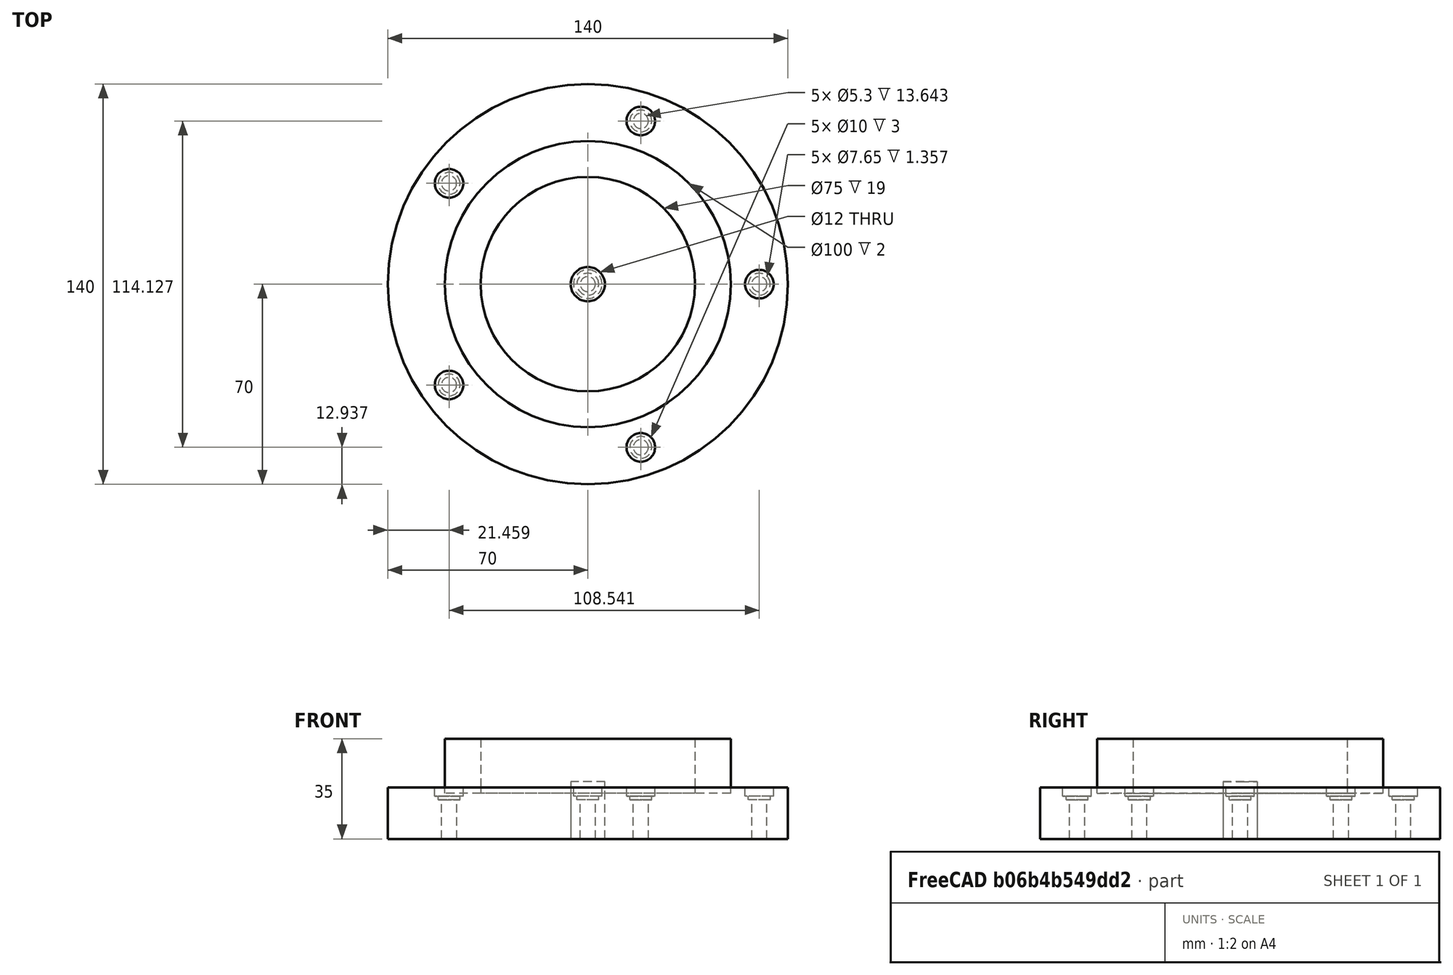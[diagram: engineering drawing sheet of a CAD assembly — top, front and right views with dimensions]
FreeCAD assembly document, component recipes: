
FREECAD ASSEMBLY — COMPONENT RECIPES ("composit_stand3_basement_bearing_holder_model")

This assembly document has 3 components, labeled P0..P2 below (a component is one placed body or linked part). 3 of them carry a construction recipe — the FreeCAD feature program that regenerates the part from scratch, quoted from this document or its linked companion documents; the rest are supplied as boundary geometry only. No exploded tour is included for this assembly.
COMPONENT P0 — recipe-attached ("Body", modeled in this document).
Construction recipe (the document's own serialized feature program — sketch geometry with constraints, then the solid features built on it; lengths are millimeters unless a unit is written):

FEATURE [Sketcher::SketchObject] Sketch
  ArcFitTolerance = 0
  AttachmentSupport = -> [XZ_Plane001]
  FullyConstrained = true
  MakeInternals = false
  MapMode = 5
  Placement = pos=(0,0,0) rot=(1,0,0;1.5708rad)
  sketch-geometry (9):
    g0: LineSegment StartX=0 StartY=0 StartZ=0 EndX=2.65 EndY=0 EndZ=0
    g1: LineSegment StartX=2.65 StartY=0 StartZ=0 EndX=2.65 EndY=13.6432 EndZ=0
    g2: LineSegment StartX=2.65 StartY=13.6432 StartZ=0 EndX=3.825 EndY=13.6432 EndZ=0
    g3: LineSegment StartX=3.825 StartY=13.6432 StartZ=0 EndX=3.825 EndY=15 EndZ=0
    g4: LineSegment StartX=3.825 StartY=15 StartZ=0 EndX=5 EndY=15 EndZ=0
    g5: LineSegment StartX=5 StartY=15 StartZ=0 EndX=5 EndY=18 EndZ=0
    g6: LineSegment StartX=5 StartY=18 StartZ=0 EndX=0 EndY=18 EndZ=0
    g7: LineSegment StartX=0 StartY=18 StartZ=0 EndX=0 EndY=0 EndZ=0
    g8: LineSegment [constr] StartX=2.65 StartY=13.6432 StartZ=0 EndX=5 EndY=15 EndZ=0
  constraints (25):
    c: Coincident(g-1,g0)
    c: Horizontal(g0)
    c: Coincident(g0,g1)
    c: Vertical(g1)
    c: Coincident(g1,g2)
    c: Horizontal(g2)
    c: Coincident(g2,g3)
    c: Vertical(g3)
    c: Coincident(g3,g4)
    c: Horizontal(g4)
    c: Coincident(g4,g5)
    c: Vertical(g5)
    c: Coincident(g5,g6)
    c: PointOnObject(g6,g-2)
    c: Horizontal(g6)
    c: Coincident(g6,g7)
    c: Coincident(g7,g0)
    c: DistanceY(g7,g7) = 18
    c: Coincident(g8,g1)
    c: Coincident(g8,g4)
    c: Angle(g8) = 0.523599
    c: Equal(g4,g2)
    c: DistanceY(g5,g5) = 3
    c: DistanceX(g0) = 2.65
    c: DistanceX(g6,g6) = 5
FEATURE [PartDesign::Revolution] Revolution
  Angle = 360
  Angle2 = 60
  Axis = (0,2e-16,1)
  Base = (0,0,0)
  Placement = pos=(0,0,0) rot=(1,0,0;1.5708rad)
  Profile = -> Sketch
  ReferenceAxis = -> Sketch [V_Axis]
  Reversed = true
  Suppressed = false
  Type = 0
FEATURE [PartDesign::Body] Body001  label="Body"
  AllowCompound = false
  Group = -> [Sketch,Revolution]
  Origin = -> Origin001
  Tip = -> Revolution
COMPONENT P1 — recipe-attached ("Body002", modeled in this document).
Construction recipe (the document's own serialized feature program — sketch geometry with constraints, then the solid features built on it; lengths are millimeters unless a unit is written):

FEATURE [PartDesign::SubShapeBinder] Binder001
  BindCopyOnChange = 0
  BindMode = 0
  ClaimChildren = true
  Context = -> Body [Binder001.]
  Fuse = false
  MakeFace = true
  OffsetFill = false
  OffsetIntersection = false
  OffsetJoinType = 0
  OffsetOpenResult = false
  PartialLoad = false
  Relative = false
  Support = -> [Binder]
  _Version = 2
FEATURE [PartDesign::Pad] Pad
  Direction = (0,0,1)
  Length = 18
  Length2 = 10
  Profile = -> Binder001
  Suppressed = false
  Type = 0
FEATURE [PartDesign::CoordinateSystem] Local_CS  label="bottom_LCS"
  AttacherType = Attacher::AttachEngine3D
  AttachmentSupport = -> [XY_Plane]
  MapMode = 5
FEATURE [PartDesign::CoordinateSystem] Local_CS001  label="top_LCS"
  AttacherType = Attacher::AttachEngine3D
  AttachmentOffset = pos=(0,0,18) rot=(0,0,1;0rad)
  AttachmentSupport = -> [XY_Plane]
  MapMode = 5
  Placement = pos=(0,0,18) rot=(0,0,1;0rad)
FEATURE [PartDesign::CoordinateSystem] Local_CS002  label="bearing_LCS"
  AttacherType = Attacher::AttachEngine3D
  AttachmentOffset = pos=(0,0,16) rot=(0,0,1;0rad)
  AttachmentSupport = -> [XY_Plane]
  MapMode = 5
  Placement = pos=(0,0,16) rot=(0,0,1;0rad)
  expr: AttachmentOffset = <<bearing_placement>>.LinkedObject.Placement
FEATURE [PartDesign::Boolean] Boolean
  BaseFeature = -> Pad
  Group = -> [Fusion]
  Suppressed = false
  Type = 1
  UsePlacement = true
FEATURE [PartDesign::Body] Body  label="bearing_holder"
  AllowCompound = false
  Group = -> [Binder001,Pad,Boolean,Local_CS,Local_CS001,Local_CS002]
  Origin = -> Origin
  Tip = -> Boolean
COMPONENT P2 — recipe-attached ("axis_bolt", a linked part whose construction recipe lives in a companion FreeCAD document of the same project; that document's serialized recipe follows).
Construction recipe (the companion document, serialized — sketch geometry with constraints, then the solid features built on it; lengths are millimeters unless a unit is written):

FCSTD DOCUMENT  (FreeCAD 1.1R38827 (Git))
Label: composit_stand3_basement_amplifier_main
License: All rights reserved
LicenseURL: http://en.wikipedia.org/wiki/All_rights_reserved
objects: Part::FeaturePython×7, PartDesign::SubShapeBinder×2, Sketcher::SketchObject×2, App::Link×1, Part::Cylinder×1, PartDesign::Revolution×1, PartDesign::Body×1
note: 18 computed .brp shape members not serialized (recipe doc carries the construction recipe); baked Part::Feature solids carry a one-line shape summary decoded from their .brp
EXTERNAL_REF file=composit_stand3_basement_bottom_main.FCStd obj=Sketch
EXTERNAL_REF file=composit_stand3_basement_top_main.FCStd obj=Sketch
EXTERNAL_REF file=composit_stand3_basement_bearing_holder_main.FCStd obj=Join

FEATURE [PartDesign::SubShapeBinder] Binder
  BindCopyOnChange = 0
  BindMode = 0
  ClaimChildren = false
  Fuse = false
  MakeFace = true
  OffsetFill = false
  OffsetIntersection = false
  OffsetJoinType = 0
  OffsetOpenResult = false
  PartialLoad = false
  Relative = true
  Support = -> [<external composit_stand3_basement_bottom_main.FCStd>#Sketch]
  _Version = 2
FEATURE [PartDesign::SubShapeBinder] Binder001
  BindCopyOnChange = 0
  BindMode = 0
  ClaimChildren = false
  Fuse = false
  MakeFace = true
  OffsetFill = false
  OffsetIntersection = false
  OffsetJoinType = 0
  OffsetOpenResult = false
  PartialLoad = false
  Relative = true
  Support = -> [<external composit_stand3_basement_top_main.FCStd>#Sketch]
  _Version = 2
FEATURE [Sketcher::SketchObject] Sketch
  ArcFitTolerance = 0
  ExternalGeometry = -> [Binder001]
  FullyConstrained = true
  MakeInternals = false
  expr: Constraints[6] = <<composit_stand3_basement_bottom_main>>#<<basement_bottom_main_sketch>>.Constraints.min_r - 20 mm
  sketch-geometry (5):
    g0: LineSegment [constr] StartX=0 StartY=0 StartZ=0 EndX=75 EndY=129.904 EndZ=0
    g1: ArcOfCircle CenterX=-272.703 CenterY=-472.335 CenterZ=0 NormalX=0 NormalY=0 NormalZ=1 AngleXU=0 Radius=695.406 StartAngle=0.871298 EndAngle=1.0472
    g2: ArcOfCircle CenterX=155.708 CenterY=36.8099 CenterZ=0 NormalX=0 NormalY=0 NormalZ=1 AngleXU=0 Radius=30 StartAngle=0.232142 EndAngle=0.871298
    g3: ArcOfCircle CenterX=0 CenterY=0 CenterZ=0 NormalX=0 NormalY=0 NormalZ=1 AngleXU=0 Radius=190 StartAngle=0 EndAngle=0.232142
    g4: Circle [constr] CenterX=0 CenterY=0 CenterZ=0 NormalX=0 NormalY=0 NormalZ=1 AngleXU=0 Radius=545.406
  constraints (14):
    c: Coincident(g0,g-1)
    c: Angle(g0) = 1.0472
    c: Coincident(g1,g0)
    c: PointOnObject(g3,g-1)
    c: Tangent(g3,g2) = -1.5708
    c: Tangent(g2,g1) = -1.5708
    c: Distance(g0) = 150
    c: Coincident(g4,g0)
    c: PointOnObject(g-3,g4)
    c: Coincident(g1,g-3)
    c: DistanceX(g3) = 190
    c: Radius(g2) = 30
    c: PointOnObject(g3,g-1)
    c: PointOnObject(g3,g-2)
FEATURE [Part::FeaturePython] Placment  # WARN: FeaturePython — macro-defined, semantics opaque (R4)
  AttacherType = Attacher::AttachEngine3D
  ExposePlacement = true
  MarkerShape = 1
  MarkerSize = 20
  NumElements = 1
  Placement = pos=(65,112.583,0) rot=(0,0,1;0rad)
  Type = lattice2AttachablePlacement.AttachablePlacement
  isLattice = 1
  expr: .Placement.Base.y = .Placement.Base.x * tan(60)
FEATURE [Part::FeaturePython] Placment001  # WARN: FeaturePython — macro-defined, semantics opaque (R4)
  AttacherType = Attacher::AttachEngine3D
  ExposePlacement = true
  MarkerShape = 1
  MarkerSize = 20
  NumElements = 1
  Placement = pos=(150,40,0) rot=(0,0,1;0rad)
  Type = lattice2AttachablePlacement.AttachablePlacement
  isLattice = 1
FEATURE [Part::FeaturePython] Mirror  label="Mirror of Placment001"  # WARN: FeaturePython — macro-defined, semantics opaque (R4)
  ExposePlacement = false
  FlipX = false
  FlipY = true
  FlipZ = false
  MarkerShape = 1
  MarkerSize = 20
  NumElements = 1
  Object = -> Placment001
  ObjectTraversal = 0
  PivotPlacement = pos=(0,0,0) rot=(0,0,1;1.0472rad)
  Type = lattice2Mirror.LatticeMirror
  isLattice = 1
FEATURE [Part::FeaturePython] Join  # WARN: FeaturePython — macro-defined, semantics opaque (R4)
  ExposePlacement = false
  Interleave = false
  Links = -> [Placment,Placment001,Mirror]
  MarkerShape = 1
  MarkerSize = 0
  NumElements = 3
  Type = lattice2JoinArrays.JoinArrays
  isLattice = 1
FEATURE [Part::FeaturePython] PolarArray  # WARN: FeaturePython — macro-defined, semantics opaque (R4)
  Alignment = 0
  AttacherType = Attacher::AttachEngine3D
  CellStart = A1
  Count = 3
  DistributionLaw = 0
  EndInclusive = false
  ExposePlacement = false
  FlipX = false
  FlipZ = false
  GeneratorMode = 0
  MarkerShape = 1
  MarkerSize = 0
  NumElements = 3
  OrientMode = 2
  Radius = 100
  Reverse = false
  SpanEnd = 360
  SpanStart = 0
  Step = 120
  Type = lattice2PolarArray2.PolarArray
  UseArcRadius = false
  UseArcRange = 0
  VSGVersion = 1
  Values = 0.0 | 120.0 | 240.0
  ValuesSource = 2
  isLattice = 1
FEATURE [Part::FeaturePython] Populate  label="Populate PolarArray with Join"  # WARN: FeaturePython — macro-defined, semantics opaque (R4)
  Copying = 0
  ExposePlacement = false
  MarkerShape = 1
  MarkerSize = 0
  NumElements = 9
  Object = -> Join
  OutputCompounding = 0
  PlacementsTo = -> PolarArray
  Referencing = 1
  Type = lattice2PopulateCopies.LatticePopulateCopies
  isLattice = 1
FEATURE [App::Link] Link  label="bearing_holes_placements"
  LinkedObject = -> <external composit_stand3_basement_bearing_holder_main.FCStd>#Join
FEATURE [Part::FeaturePython] Join001  label="holes_placements"  # WARN: FeaturePython — macro-defined, semantics opaque (R4)
  ExposePlacement = false
  Interleave = false
  Links = -> [Populate,Link]
  MarkerShape = 1
  MarkerSize = 0
  NumElements = 14
  Type = lattice2JoinArrays.JoinArrays
  isLattice = 1
FEATURE [Part::Cylinder] Cylinder  label="axis_bolt"
  Angle = 360
  AttacherType = Attacher::AttachEngine3D
  FirstAngle = 0
  Height = 20
  Radius = 6
  SecondAngle = 0
FEATURE [Sketcher::SketchObject] Sketch001
  ArcFitTolerance = 0
  AttachmentSupport = -> [XZ_Plane]
  FullyConstrained = true
  MakeInternals = false
  MapMode = 5
  Placement = pos=(0,0,0) rot=(1,0,0;1.5708rad)
  sketch-geometry (9):
    g0: LineSegment StartX=0 StartY=0 StartZ=0 EndX=2.65 EndY=0 EndZ=0
    g1: LineSegment StartX=2.65 StartY=0 StartZ=0 EndX=2.65 EndY=14.6432 EndZ=0
    g2: LineSegment StartX=2.65 StartY=14.6432 StartZ=0 EndX=3.825 EndY=14.6432 EndZ=0
    g3: LineSegment StartX=3.825 StartY=14.6432 StartZ=0 EndX=3.825 EndY=16 EndZ=0
    g4: LineSegment StartX=3.825 StartY=16 StartZ=0 EndX=5 EndY=16 EndZ=0
    g5: LineSegment StartX=5 StartY=16 StartZ=0 EndX=5 EndY=18 EndZ=0
    g6: LineSegment StartX=5 StartY=18 StartZ=0 EndX=0 EndY=18 EndZ=0
    g7: LineSegment StartX=0 StartY=18 StartZ=0 EndX=0 EndY=0 EndZ=0
    g8: LineSegment [constr] StartX=2.65 StartY=14.6432 StartZ=0 EndX=5 EndY=16 EndZ=0
  constraints (25):
    c: Coincident(g-1,g0)
    c: PointOnObject(g0,g-1)
    c: Coincident(g0,g1)
    c: Vertical(g1)
    c: Coincident(g1,g2)
    c: Horizontal(g2)
    c: Coincident(g2,g3)
    c: Vertical(g3)
    c: Coincident(g3,g4)
    c: Horizontal(g4)
    c: Coincident(g4,g5)
    c: Vertical(g5)
    c: Coincident(g5,g6)
    c: Horizontal(g6)
    c: Coincident(g6,g7)
    c: Coincident(g7,g0)
    c: Vertical(g7)
    c: DistanceX(g0) = 2.65
    c: Coincident(g8,g1)
    c: Coincident(g8,g4)
    c: Angle(g8) = 0.523599
    c: Equal(g4,g2)
    c: DistanceY(g5,g5) = 2
    c: DistanceX(g5) = 5
    c: DistanceY(g6) = 18
FEATURE [PartDesign::Revolution] Revolution
  Angle = 360
  Angle2 = 60
  Axis = (0,2e-16,1)
  Base = (0,0,0)
  Placement = pos=(0,0,0) rot=(1,0,0;1.5708rad)
  Profile = -> Sketch001
  ReferenceAxis = -> Sketch001 [V_Axis]
  Reversed = true
  Suppressed = false
  Type = 0
FEATURE [PartDesign::Body] Body  label="screw"
  AllowCompound = false
  Group = -> [Sketch001,Revolution]
  Origin = -> Origin
  Tip = -> Revolution
PROVENANCE & LICENSES
A FreeCAD (.FCStd) document from a public repository crawl; recipes are the document's own serialized feature recipes (and, for linked parts, companion documents' recipes).
License: as declared in the source repository (recorded in the dataset sidecar).
